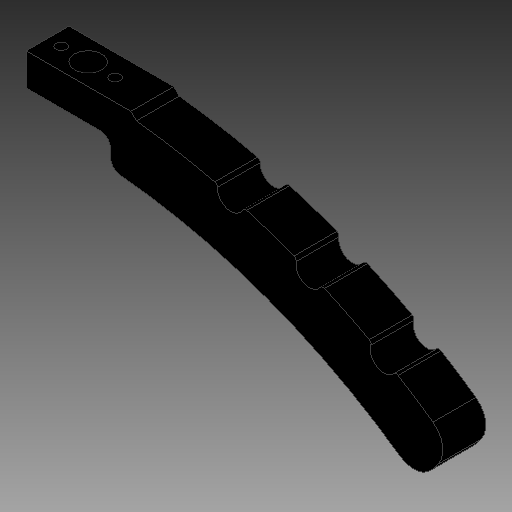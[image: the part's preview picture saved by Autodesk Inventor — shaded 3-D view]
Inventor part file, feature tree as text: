
AUTODESK INVENTOR PART (.ipt)
format: ipt  version: 2019 (Build 230136000, 136)  size: 176,640 bytes
history: native  units: mm
features: other x4, hole x2, extrude x1, pattern_circular x1, fillet x1
ambient origin geometry x8: Origin, YZ Plane, XZ Plane, XY Plane, X Axis, Y Axis, Z Axis, Center Point
bodies: Solid1 (feature_tree), Body (feature_tree)
feature tree (9):
  hole  "Dowel Pin Holes"  [1 undecoded]
  hole  "Fastening Hole"  [1 undecoded]
  extrude  "Thumbscrew Cutout"  TaperAngle=0.0deg  [1 undecoded]
  pattern_circular  "Thumbscrew Cutout Pattern"  [2 undecoded]
  fillet  "Body Fillet"  Radius=171.0mm
  other  "Body Outline"
  other  "Dowel Pin Hole Positions"
  other  "Fastening Hole Position"
  other  "Thumbscrew Cutout Outline"
note: 5 required parameter values undecoded (feature->parameter linkage not recoverable at this tier; creation-order binding heuristic only, values carry confidence <= 0.55)
